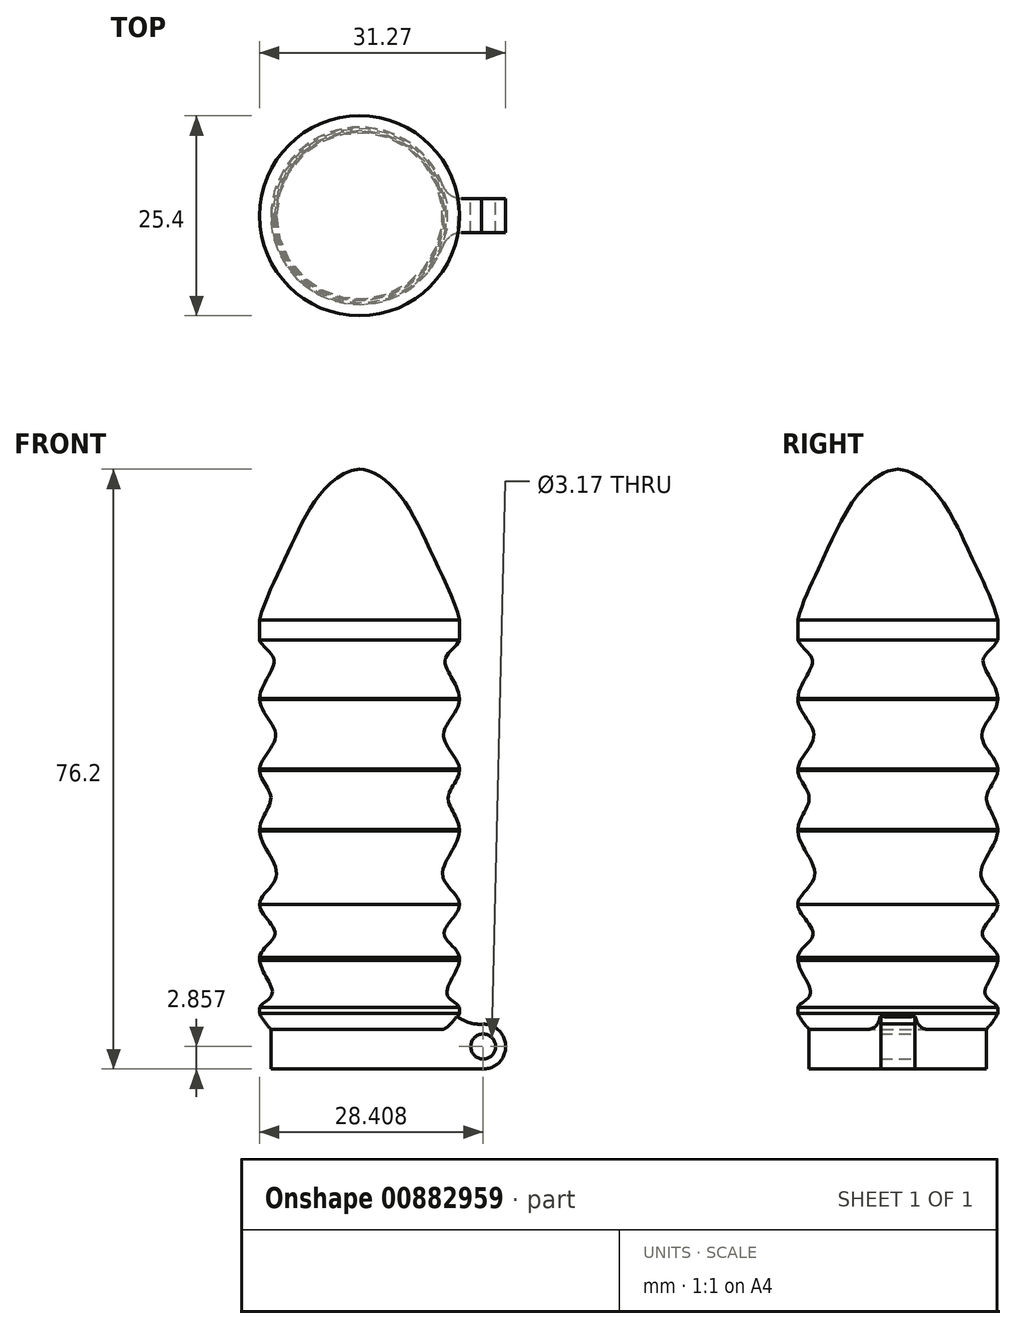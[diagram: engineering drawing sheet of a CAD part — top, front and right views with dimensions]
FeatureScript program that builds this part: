
annotation { "Feature Type Name" : "Feature", "Feature Type Description" : "" }
export const myFeature = defineFeature(function(context is Context, id is Id, definition is map)
    precondition{}
    {
        {
            var Q0;
            Q0=qCreatedBy(makeId("Front.planeOp"),FACE);
            var sketch = newSketch(context, id + "F0", { "sketchPlane" : qUnion([Q0])});
            skLineSegment(sketch, "E0.bottom", {"start": v(0, 0) * mm, "end": v(12.7, 0) * mm});
            skLineSegment(sketch, "E0.top", {"start": v(0, 76.2) * mm, "end": v(12.7, 76.2) * mm});
            skLineSegment(sketch, "E0.left", {"start": v(0, 0) * mm, "end": v(0, 76.2) * mm});
            skLineSegment(sketch, "E0.right", {"start": v(12.7, 0) * mm, "end": v(12.7, 76.2) * mm});
            skFitSpline(sketch, "E1", {"points": [v(0, 76.2) * mm, v(4.32, 73.83) * mm, v(9.9, 63.95) * mm, v(12.7, 54.53) * mm, v(10.84, 51.9) * mm, v(12.7, 46.97) * mm, v(10.66, 42.38) * mm, v(12.7, 38.1) * mm, v(11.26, 34.46) * mm, v(12.7, 30.23) * mm, v(10.56, 24.59) * mm, v(12.7, 20.89) * mm, v(10.73, 17.19) * mm, v(12.7, 14.2) * mm, v(11.09, 9.6) * mm, v(12.7, 7.85) * mm, v(11.26, 5.03) * mm], "startDerivative": vector(56.15, 0) * mm, "endDerivative": vector(-57.3, -68.53) * mm});
            skLineSegment(sketch, "E2", {"start": v(11.26, 5.03) * mm, "end": v(11.26, 0) * mm});
            skSolve(sketch);
        }
        {
            var Q0;
            {var subQ1=sQuery(id+"F0.wireOp",EDGE,"E0.left");Q0=makeQuery(id+"F0.imprint","IMPRINT",FACE,{"disambiguationData":[TD([[makeQuery(id+"F0.imprint","IMPRINT",EDGE,{"derivedFrom":subQ1}),-1.0]])]});}
            var Q1;
            Q1=sQuery(id+"F0.wireOp",EDGE,"E0.left");
            revolve(context, id + "F1", {"surfaceOperationType" : NewSurfaceOperationType.NEW, "entities" : qUnion([Q0]), "axis" : qUnion([Q1]), "revolveType" : RevolveType.FULL});
        }
        {
            var Q0;
            Q0=qCreatedBy(makeId("Front.planeOp"),FACE);
            var sketch = newSketch(context, id + "F2", { "sketchPlane" : qUnion([Q0])});
            skCircle(sketch, "E3", {"center": v(15.7, 2.86) * mm, "radius": 1.59 * mm});
            skCircle(sketch, "E4.0", {"center": v(15.7, 2.86) * mm, "radius": 2.86 * mm});
            skLineSegment(sketch, "E5", {"start": v(-11.26, 0) * mm, "end": v(-11.26, 5.03) * mm});
            skLineSegment(sketch, "E6", {"start": v(11.26, 5.03) * mm, "end": v(11.26, 0) * mm});
            skLineSegment(sketch, "E7", {"start": v(12.7, 7.85) * mm, "end": v(12.7, 7.12) * mm});
            skPoint(sketch, "E8.start.orphan", {"position": v(15.7, 0) * mm});
            skLineSegment(sketch, "E9", {"start": v(15.7, 0) * mm, "end": v(8.93, 0) * mm});
            skFitSpline(sketch, "E10", {"points": [v(15.7, 5.72) * mm, v(13.76, 5.96) * mm, v(10.05, 8.57) * mm, v(8.93, 10.66) * mm], "startDerivative": vector(-6.34, -0.25) * mm, "endDerivative": vector(-2.4, 6.65) * mm});
            skLineSegment(sketch, "E11", {"start": v(8.93, 10.66) * mm, "end": v(8.93, 0) * mm});
            skSolve(sketch);
        }
        {
            var Q0;
            Q0 = qSketchRegion(id + "F2", true);
            extrude(context, id + "F3", {"entities" : qUnion([Q0]), "operationType" : NewBodyOperationType.ADD, "depth" : 2.16 * mm, "offsetDistance" : 25.4 * mm, "hasSecondDirection" : true, "secondDirectionOppositeDirection" : true, "secondDirectionDepth" : 2.16 * mm});
        }
        {
            var Q0;
            Q0=makeQuery(id+"F3.boolean.opBoolean","INTERSECT",EDGE,{"derivedFrom":[makeQuery(id+"F1.opRevolve","SWEPT_FACE",FACE,{"disambiguationData":[OSD([sQuery(id+"F0.wireOp",EDGE,"E2")])]}),makeQuery(id+"F3.opExtrude","CAP_FACE",FACE,{"disambiguationData":[OSD([sQuery(id+"F2.wireOp",EDGE,"E3"),sQuery(id+"F2.wireOp",EDGE,"E4.0"),sQuery(id+"F2.wireOp",EDGE,"E9"),sQuery(id+"F2.wireOp",EDGE,"E10"),sQuery(id+"F2.wireOp",EDGE,"E11")])],"isStart":false})]});
            var Q1;
            Q1=makeQuery(id+"F3.boolean.opBoolean","INTERSECT",EDGE,{"derivedFrom":[makeQuery(id+"F1.opRevolve","SWEPT_FACE",FACE,{"disambiguationData":[OSD([sQuery(id+"F0.wireOp",EDGE,"E2")])]}),makeQuery(id+"F3.opExtrude","CAP_FACE",FACE,{"disambiguationData":[OSD([sQuery(id+"F2.wireOp",EDGE,"E3"),sQuery(id+"F2.wireOp",EDGE,"E4.0"),sQuery(id+"F2.wireOp",EDGE,"E9"),sQuery(id+"F2.wireOp",EDGE,"E10"),sQuery(id+"F2.wireOp",EDGE,"E11")])],"isStart":true})]});
            fillet(context, id + "F4", {"entities" : qUnion([Q0, Q1]), "radius" : 2.54 * mm, "tangentPropagation" : true, "allowEdgeOverflow" : false});
        }
    });
